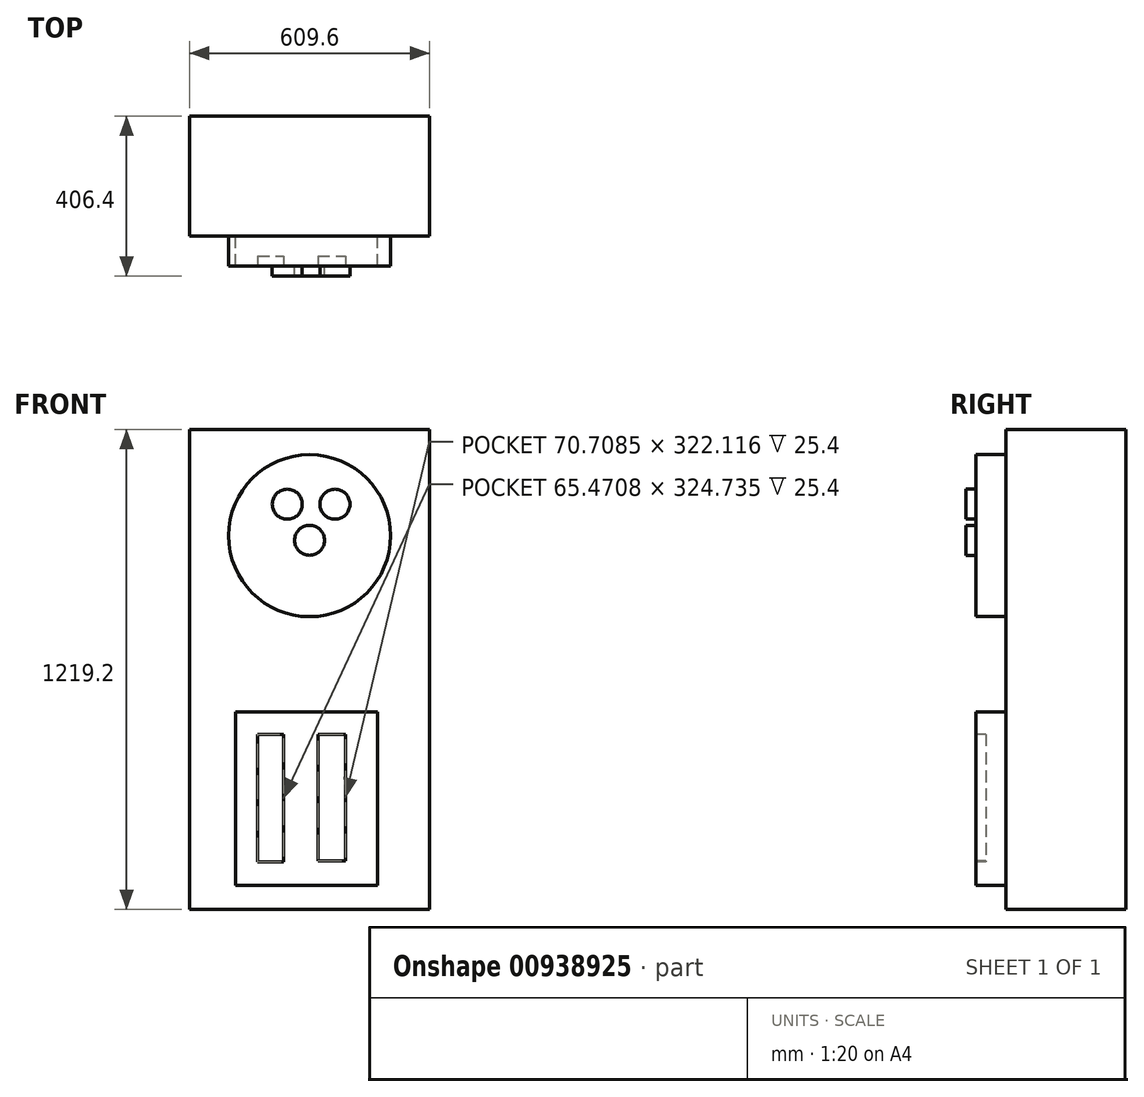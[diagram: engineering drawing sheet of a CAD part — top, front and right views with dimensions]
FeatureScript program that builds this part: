
annotation { "Feature Type Name" : "Feature", "Feature Type Description" : "" }
export const myFeature = defineFeature(function(context is Context, id is Id, definition is map)
    precondition{}
    {
        {
            var Q0;
            Q0=qCreatedBy(makeId("Front.planeOp"),FACE);
            var sketch = newSketch(context, id + "F0", { "sketchPlane" : qUnion([Q0])});
            skLineSegment(sketch, "E0.bottom", {"start": v(-304.8, 609.6) * mm, "end": v(304.8, 609.6) * mm});
            skLineSegment(sketch, "E0.top", {"start": v(-304.8, -609.6) * mm, "end": v(304.8, -609.6) * mm});
            skLineSegment(sketch, "E0.left", {"start": v(-304.8, 609.6) * mm, "end": v(-304.8, -609.6) * mm});
            skLineSegment(sketch, "E0.right", {"start": v(304.8, 609.6) * mm, "end": v(304.8, -609.6) * mm});
            skPoint(sketch, "E0.middle", {"position": v(0, 0) * mm});
            skSolve(sketch);
        }
        {
            var Q0;
            Q0=makeQuery(id+"F0.imprint","IMPRINT",FACE,{"disambiguationData":[TD([[makeQuery(id+"F0.imprint","IMPRINT",EDGE,{"derivedFrom":sQuery(id+"F0.wireOp",EDGE,"E0.bottom")}),-1.0]])]});
            extrude(context, id + "F1", {"entities" : qUnion([Q0]), "depth" : 304.8 * mm, "offsetDistance" : 25.4 * mm});
        }
        {
            var Q0;
            Q0=makeQuery(id+"F1.opExtrude","CAP_FACE",FACE,{"disambiguationData":[OSD([sQuery(id+"F0.wireOp",EDGE,"E0.bottom"),sQuery(id+"F0.wireOp",EDGE,"E0.top"),sQuery(id+"F0.wireOp",EDGE,"E0.left"),sQuery(id+"F0.wireOp",EDGE,"E0.right")])],"isStart":false});
            var sketch = newSketch(context, id + "F2", { "sketchPlane" : qUnion([Q0])});
            skCircle(sketch, "E1", {"center": v(0, 340) * mm, "radius": 205.82 * mm});
            skSolve(sketch);
        }
        {
            var Q0;
            Q0=makeQuery(id+"F2.imprint","IMPRINT",FACE,{"disambiguationData":[TD([[makeQuery(id+"F2.imprint","IMPRINT",EDGE,{"derivedFrom":sQuery(id+"F2.wireOp",EDGE,"E1")}),1.0]])]});
            extrude(context, id + "F3", {"entities" : qUnion([Q0]), "operationType" : NewBodyOperationType.ADD, "depth" : 76.2 * mm, "offsetDistance" : 25.4 * mm});
        }
        {
            var Q0;
            Q0=makeQuery(id+"F2.imprint","IMPRINT",FACE,{"disambiguationData":[TD([[makeQuery(id+"F2.imprint","IMPRINT",EDGE,{"derivedFrom":sQuery(id+"F2.wireOp",EDGE,"E1")}),-1.0]])]});
            var sketch = newSketch(context, id + "F4", { "sketchPlane" : qUnion([Q0])});
            skLineSegment(sketch, "E2.bottom", {"start": v(-188.03, -108.18) * mm, "end": v(172.58, -108.18) * mm});
            skLineSegment(sketch, "E2.top", {"start": v(-188.03, -548.64) * mm, "end": v(172.58, -548.64) * mm});
            skLineSegment(sketch, "E2.left", {"start": v(-188.03, -108.18) * mm, "end": v(-188.03, -548.64) * mm});
            skLineSegment(sketch, "E2.right", {"start": v(172.58, -108.18) * mm, "end": v(172.58, -548.64) * mm});
            skSolve(sketch);
        }
        {
            var Q0;
            Q0=makeQuery(id+"F4.imprint","IMPRINT",FACE,{"disambiguationData":[TD([[makeQuery(id+"F4.imprint","IMPRINT",EDGE,{"derivedFrom":sQuery(id+"F4.wireOp",EDGE,"E2.bottom")}),-1.0]])]});
            extrude(context, id + "F5", {"entities" : qUnion([Q0]), "operationType" : NewBodyOperationType.ADD, "depth" : 76.2 * mm, "offsetDistance" : 25.4 * mm});
        }
        {
            var Q0;
            Q0=makeQuery(id+"F3.opExtrude","CAP_FACE",FACE,{"disambiguationData":[OSD([sQuery(id+"F2.wireOp",EDGE,"E1")])],"isStart":false});
            var sketch = newSketch(context, id + "F6", { "sketchPlane" : qUnion([Q0])});
            skCircle(sketch, "E3", {"center": v(-56.67, 419.85) * mm, "radius": 38.1 * mm});
            skSolve(sketch);
        }
        {
            var Q0;
            Q0=makeQuery(id+"F6.imprint","IMPRINT",FACE,{"disambiguationData":[TD([[makeQuery(id+"F6.imprint","IMPRINT",EDGE,{"derivedFrom":sQuery(id+"F6.wireOp",EDGE,"E3")}),-1.0]])]});
            var sketch = newSketch(context, id + "F7", { "sketchPlane" : qUnion([Q0])});
            skCircle(sketch, "E4", {"center": v(64.4, 419.85) * mm, "radius": 38.1 * mm});
            skSolve(sketch);
        }
        {
            var Q0;
            Q0=makeQuery(id+"F6.imprint","IMPRINT",FACE,{"disambiguationData":[TD([[makeQuery(id+"F6.imprint","IMPRINT",EDGE,{"derivedFrom":sQuery(id+"F6.wireOp",EDGE,"E3")}),-1.0]])]});
            var sketch = newSketch(context, id + "F8", { "sketchPlane" : qUnion([Q0])});
            skCircle(sketch, "E5", {"center": v(0, 328.25) * mm, "radius": 38.1 * mm});
            skSolve(sketch);
        }
        {
            var Q0;
            Q0=makeQuery(id+"F6.imprint","IMPRINT",FACE,{"disambiguationData":[TD([[makeQuery(id+"F6.imprint","IMPRINT",EDGE,{"derivedFrom":sQuery(id+"F6.wireOp",EDGE,"E3")}),1.0]])]});
            extrude(context, id + "F9", {"entities" : qUnion([Q0]), "depth" : 25.4 * mm, "offsetDistance" : 25.4 * mm});
        }
        {
            var Q0;
            Q0=makeQuery(id+"F7.imprint","IMPRINT",FACE,{"disambiguationData":[TD([[makeQuery(id+"F7.imprint","IMPRINT",EDGE,{"derivedFrom":sQuery(id+"F7.wireOp",EDGE,"E4")}),1.0]])]});
            extrude(context, id + "F10", {"entities" : qUnion([Q0]), "depth" : 25.4 * mm, "offsetDistance" : 25.4 * mm});
        }
        {
            var Q0;
            Q0=makeQuery(id+"F8.imprint","IMPRINT",FACE,{"disambiguationData":[TD([[makeQuery(id+"F8.imprint","IMPRINT",EDGE,{"derivedFrom":sQuery(id+"F8.wireOp",EDGE,"E5")}),1.0]])]});
            extrude(context, id + "F11", {"entities" : qUnion([Q0]), "depth" : 25.4 * mm, "offsetDistance" : 25.4 * mm});
        }
        {
            var Q0;
            Q0=makeQuery(id+"F5.opExtrude","CAP_FACE",FACE,{"disambiguationData":[OSD([sQuery(id+"F4.wireOp",EDGE,"E2.bottom"),sQuery(id+"F4.wireOp",EDGE,"E2.top"),sQuery(id+"F4.wireOp",EDGE,"E2.left"),sQuery(id+"F4.wireOp",EDGE,"E2.right")])],"isStart":false});
            var sketch = newSketch(context, id + "F12", { "sketchPlane" : qUnion([Q0])});
            skLineSegment(sketch, "E6.bottom", {"start": v(-132.12, -164.73) * mm, "end": v(-66.65, -164.73) * mm});
            skLineSegment(sketch, "E6.top", {"start": v(-132.12, -489.47) * mm, "end": v(-66.65, -489.47) * mm});
            skLineSegment(sketch, "E6.left", {"start": v(-132.12, -164.73) * mm, "end": v(-132.12, -489.47) * mm});
            skLineSegment(sketch, "E6.right", {"start": v(-66.65, -164.73) * mm, "end": v(-66.65, -489.47) * mm});
            skLineSegment(sketch, "E7.bottom", {"start": v(21.08, -164.73) * mm, "end": v(91.79, -164.73) * mm});
            skLineSegment(sketch, "E7.top", {"start": v(21.08, -486.85) * mm, "end": v(91.79, -486.85) * mm});
            skLineSegment(sketch, "E7.left", {"start": v(91.79, -164.73) * mm, "end": v(91.79, -486.85) * mm});
            skLineSegment(sketch, "E7.right", {"start": v(21.08, -164.73) * mm, "end": v(21.08, -486.85) * mm});
            skSolve(sketch);
        }
        {
            var Q0;
            Q0=makeQuery(id+"F12.imprint","IMPRINT",FACE,{"disambiguationData":[TD([[makeQuery(id+"F12.imprint","IMPRINT",EDGE,{"derivedFrom":sQuery(id+"F12.wireOp",EDGE,"E6.bottom")}),-1.0]])]});
            var Q1;
            Q1=makeQuery(id+"F12.imprint","IMPRINT",FACE,{"disambiguationData":[TD([[makeQuery(id+"F12.imprint","IMPRINT",EDGE,{"derivedFrom":sQuery(id+"F12.wireOp",EDGE,"E7.bottom")}),-1.0]])]});
            extrude(context, id + "F13", {"entities" : qUnion([Q0, Q1]), "operationType" : NewBodyOperationType.REMOVE, "oppositeDirection" : true, "depth" : 25.4 * mm, "offsetDistance" : 25.4 * mm});
        }
    });
